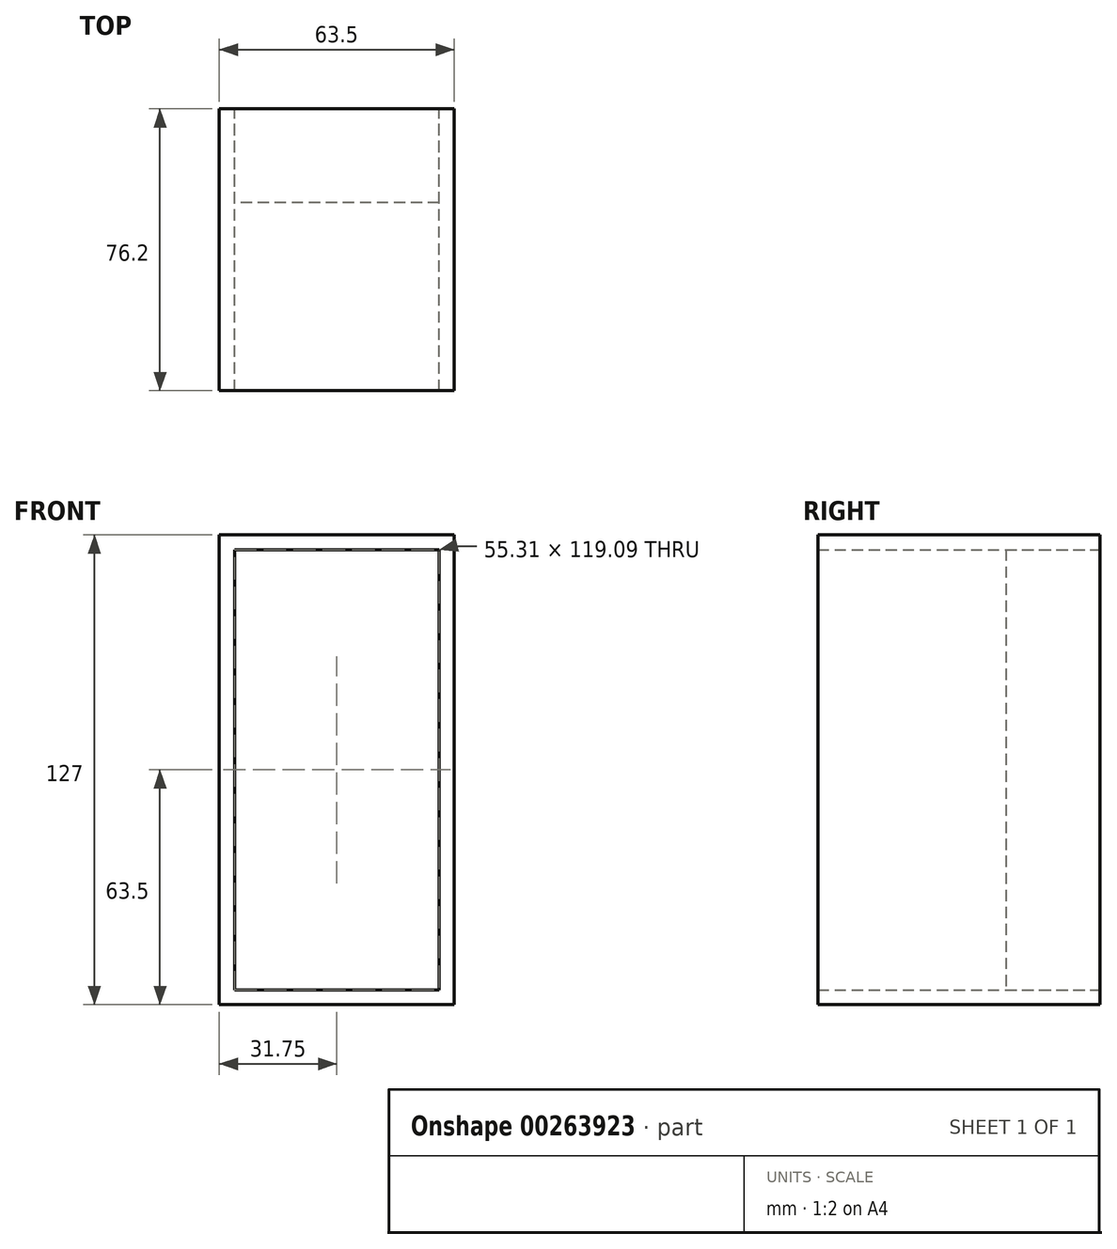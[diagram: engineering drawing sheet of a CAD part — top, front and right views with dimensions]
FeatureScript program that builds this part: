
annotation { "Feature Type Name" : "Feature", "Feature Type Description" : "" }
export const myFeature = defineFeature(function(context is Context, id is Id, definition is map)
    precondition{}
    {
        {
            var Q0;
            Q0=qCreatedBy(makeId("Front.planeOp"),FACE);
            var sketch = newSketch(context, id + "F0", { "sketchPlane" : qUnion([Q0])});
            skLineSegment(sketch, "E0.bottom", {"start": v(31.75, 63.5) * mm, "end": v(-31.75, 63.5) * mm});
            skLineSegment(sketch, "E0.top", {"start": v(31.75, -63.5) * mm, "end": v(-31.75, -63.5) * mm});
            skLineSegment(sketch, "E0.left", {"start": v(31.75, 63.5) * mm, "end": v(31.75, -63.5) * mm});
            skLineSegment(sketch, "E0.right", {"start": v(-31.75, 63.5) * mm, "end": v(-31.75, -63.5) * mm});
            skPoint(sketch, "E0.middle", {"position": v(0, 0) * mm});
            skLineSegment(sketch, "E1.bottom", {"start": v(27.65, 59.55) * mm, "end": v(-27.65, 59.55) * mm});
            skLineSegment(sketch, "E1.top", {"start": v(27.65, -59.55) * mm, "end": v(-27.65, -59.55) * mm});
            skLineSegment(sketch, "E1.left", {"start": v(27.65, 59.55) * mm, "end": v(27.65, -59.55) * mm});
            skLineSegment(sketch, "E1.right", {"start": v(-27.65, 59.55) * mm, "end": v(-27.65, -59.55) * mm});
            skSolve(sketch);
        }
        {
            var Q0;
            Q0 = qSketchRegion(id + "F0", true);
            extrude(context, id + "F1", {"entities" : qUnion([Q0]), "depth" : 76.2 * mm});
        }
        {
            var Q0;
            Q0=makeQuery(id+"F0.imprint","IMPRINT",FACE,{"disambiguationData":[TD([[makeQuery(id+"F0.imprint","IMPRINT",EDGE,{"derivedFrom":sQuery(id+"F0.wireOp",EDGE,"E1.bottom")}),1.0]])]});
            extrude(context, id + "F2", {"entities" : qUnion([Q0]), "depth" : 25.4 * mm});
        }
    });
